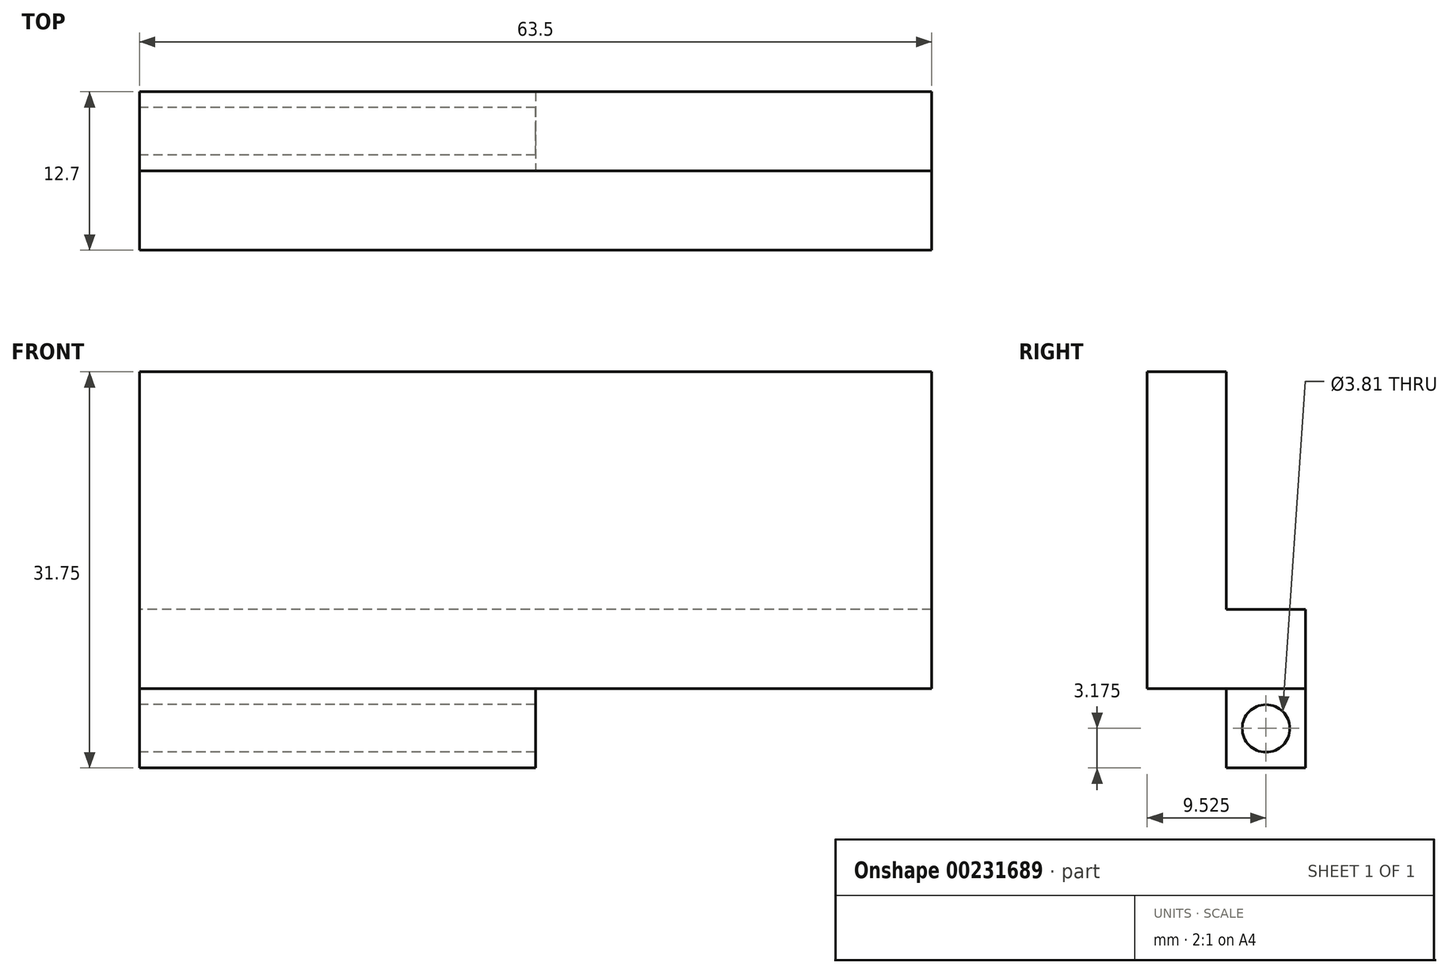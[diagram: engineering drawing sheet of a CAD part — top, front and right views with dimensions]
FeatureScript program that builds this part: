
annotation { "Feature Type Name" : "Feature", "Feature Type Description" : "" }
export const myFeature = defineFeature(function(context is Context, id is Id, definition is map)
    precondition{}
    {
        {
            var Q0;
            Q0=qCreatedBy(makeId("Front.planeOp"),FACE);
            var sketch = newSketch(context, id + "F0", { "sketchPlane" : qUnion([Q0])});
            skLineSegment(sketch, "E0.bottom", {"start": v(0, 0) * mm, "end": v(-63.5, 0) * mm});
            skLineSegment(sketch, "E0.top", {"start": v(0, 25.4) * mm, "end": v(-63.5, 25.4) * mm});
            skLineSegment(sketch, "E0.left", {"start": v(0, 0) * mm, "end": v(0, 25.4) * mm});
            skLineSegment(sketch, "E0.right", {"start": v(-63.5, 0) * mm, "end": v(-63.5, 25.4) * mm});
            skSolve(sketch);
        }
        {
            var Q0;
            Q0=makeQuery(id+"F0.imprint","IMPRINT",FACE,{"disambiguationData":[TD([[makeQuery(id+"F0.imprint","IMPRINT",EDGE,{"derivedFrom":sQuery(id+"F0.wireOp",EDGE,"E0.bottom")}),-1.0]])]});
            extrude(context, id + "F1", {"entities" : qUnion([Q0]), "depth" : 6.35 * mm});
        }
        {
            var Q0;
            Q0=qCreatedBy(makeId("Front.planeOp"),FACE);
            var sketch = newSketch(context, id + "F2", { "sketchPlane" : qUnion([Q0])});
            skLineSegment(sketch, "E1.bottom", {"start": v(0, 0) * mm, "end": v(-63.5, 0) * mm});
            skLineSegment(sketch, "E1.top", {"start": v(0, 6.35) * mm, "end": v(-63.5, 6.35) * mm});
            skLineSegment(sketch, "E1.left", {"start": v(0, 0) * mm, "end": v(0, 6.35) * mm});
            skLineSegment(sketch, "E1.right", {"start": v(-63.5, 0) * mm, "end": v(-63.5, 6.35) * mm});
            skSolve(sketch);
        }
        {
            var Q0;
            Q0=makeQuery(id+"F2.imprint","IMPRINT",FACE,{"disambiguationData":[TD([[makeQuery(id+"F2.imprint","IMPRINT",EDGE,{"derivedFrom":sQuery(id+"F2.wireOp",EDGE,"E1.bottom")}),-1.0]])]});
            extrude(context, id + "F3", {"entities" : qUnion([Q0]), "operationType" : NewBodyOperationType.ADD, "oppositeDirection" : true, "depth" : 6.35 * mm});
        }
        {
            var Q0;
            Q0=makeQuery(id+"F3.boolean.opBoolean","MERGE",FACE,{"derivedFrom":[makeQuery(id+"F1.opExtrude","SWEPT_FACE",FACE,{"disambiguationData":[OSD([sQuery(id+"F0.wireOp",EDGE,"E0.bottom")])]}),makeQuery(id+"F3.opExtrude","SWEPT_FACE",FACE,{"disambiguationData":[OSD([sQuery(id+"F2.wireOp",EDGE,"E1.bottom")])]})]});
            var sketch = newSketch(context, id + "F4", { "sketchPlane" : qUnion([Q0])});
            skLineSegment(sketch, "E2.bottom", {"start": v(0, 0) * mm, "end": v(-63.5, 0) * mm});
            skLineSegment(sketch, "E2.top", {"start": v(0, -6.35) * mm, "end": v(-63.5, -6.35) * mm});
            skLineSegment(sketch, "E2.left", {"start": v(0, 0) * mm, "end": v(0, -6.35) * mm});
            skLineSegment(sketch, "E2.right", {"start": v(-63.5, 0) * mm, "end": v(-63.5, -6.35) * mm});
            skSolve(sketch);
        }
        {
            var Q0;
            Q0=makeQuery(id+"F4.imprint","IMPRINT",FACE,{"disambiguationData":[TD([[makeQuery(id+"F4.imprint","IMPRINT",EDGE,{"derivedFrom":sQuery(id+"F4.wireOp",EDGE,"E2.bottom")}),1.0]])]});
            extrude(context, id + "F5", {"entities" : qUnion([Q0]), "operationType" : NewBodyOperationType.ADD, "depth" : 6.35 * mm});
        }
        {
            var Q0;
            Q0=makeQuery(id+"F5.boolean.opBoolean","MERGE",FACE,{"derivedFrom":[makeQuery(id+"F3.boolean.opBoolean","MERGE",FACE,{"derivedFrom":[makeQuery(id+"F1.opExtrude","SWEPT_FACE",FACE,{"disambiguationData":[OSD([sQuery(id+"F0.wireOp",EDGE,"E0.right")])]}),makeQuery(id+"F3.opExtrude","SWEPT_FACE",FACE,{"disambiguationData":[OSD([sQuery(id+"F2.wireOp",EDGE,"E1.right")])]})]}),makeQuery(id+"F5.opExtrude","SWEPT_FACE",FACE,{"disambiguationData":[OSD([sQuery(id+"F4.wireOp",EDGE,"E2.right")])]})]});
            var sketch = newSketch(context, id + "F6", { "sketchPlane" : qUnion([Q0])});
            skCircle(sketch, "E3", {"center": v(-3.17, -3.17) * mm, "radius": 1.9 * mm});
            skPoint(sketch, "E3.centerSnap0", {"position": v(0, -3.17) * mm});
            skSolve(sketch);
        }
        {
            var Q0;
            Q0=makeQuery(id+"F6.imprint","IMPRINT",FACE,{"disambiguationData":[TD([[makeQuery(id+"F6.imprint","IMPRINT",EDGE,{"derivedFrom":sQuery(id+"F6.wireOp",EDGE,"E3")}),1.0]])]});
            extrude(context, id + "F7", {"entities" : qUnion([Q0]), "operationType" : NewBodyOperationType.REMOVE, "endBound" : BoundingType.THROUGH_ALL, "oppositeDirection" : true, "depth" : 25.4 * mm});
        }
        {
            var Q0;
            Q0=makeQuery(id+"F5.opExtrude","SWEPT_FACE",FACE,{"disambiguationData":[OSD([sQuery(id+"F4.wireOp",EDGE,"E2.bottom")])]});
            var sketch = newSketch(context, id + "F8", { "sketchPlane" : qUnion([Q0])});
            skLineSegment(sketch, "E4.bottom", {"start": v(0, 0) * mm, "end": v(-31.75, 0) * mm});
            skLineSegment(sketch, "E4.top", {"start": v(0, -6.35) * mm, "end": v(-31.75, -6.35) * mm});
            skLineSegment(sketch, "E4.left", {"start": v(0, 0) * mm, "end": v(0, -6.35) * mm});
            skLineSegment(sketch, "E4.right", {"start": v(-31.75, 0) * mm, "end": v(-31.75, -6.35) * mm});
            skSolve(sketch);
        }
        {
            var Q0;
            Q0=makeQuery(id+"F8.imprint","IMPRINT",FACE,{"disambiguationData":[TD([[makeQuery(id+"F8.imprint","IMPRINT",EDGE,{"derivedFrom":sQuery(id+"F8.wireOp",EDGE,"E4.bottom")}),1.0]])]});
            extrude(context, id + "F9", {"entities" : qUnion([Q0]), "operationType" : NewBodyOperationType.REMOVE, "oppositeDirection" : true, "depth" : 25.4 * mm});
        }
    });
